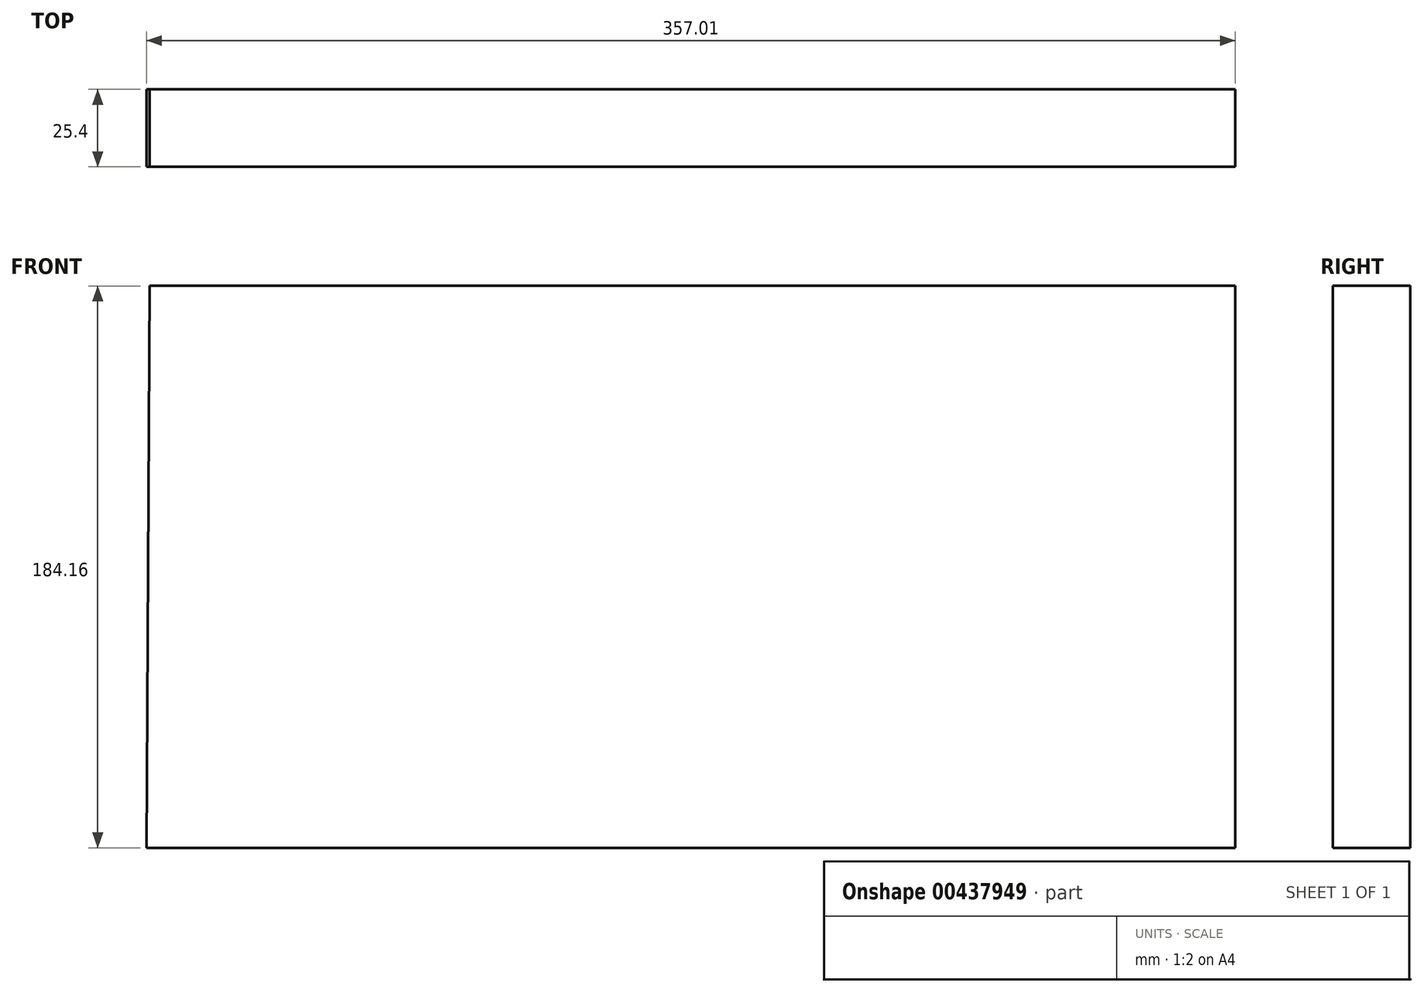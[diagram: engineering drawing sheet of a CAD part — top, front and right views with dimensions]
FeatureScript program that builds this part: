
annotation { "Feature Type Name" : "Feature", "Feature Type Description" : "" }
export const myFeature = defineFeature(function(context is Context, id is Id, definition is map)
    precondition{}
    {
        {
            var Q0;
            Q0=qCreatedBy(makeId("Front.planeOp"),FACE);
            var sketch = newSketch(context, id + "F0", { "sketchPlane" : qUnion([Q0])});
            skLineSegment(sketch, "E0.bottom", {"start": v(-163.17, 91.73) * mm, "end": v(192.83, 91.73) * mm});
            skLineSegment(sketch, "E0.top", {"start": v(-164.18, -92.43) * mm, "end": v(192.83, -92.43) * mm});
            skLineSegment(sketch, "E0.right", {"start": v(192.83, 91.73) * mm, "end": v(192.83, -92.43) * mm});
            skLineSegment(sketch, "E1", {"start": v(-163.17, 91.73) * mm, "end": v(-164.18, -92.43) * mm});
            skSolve(sketch);
        }
        {
            var Q0;
            {var subQ0=sQuery(id+"F0.wireOp",EDGE,"E0.bottom");Q0=makeQuery(id+"F0.imprint","IMPRINT",FACE,{"disambiguationData":[TD([[makeQuery(id+"F0.imprint","IMPRINT",EDGE,{"derivedFrom":subQ0}),-1.0]])]});}
            var sketch = newSketch(context, id + "F1", { "sketchPlane" : qUnion([Q0])});
            skSolve(sketch);
        }
        {
            var Q0;
            Q0 = qSketchRegion(id + "F1", true);
            var Q1;
            {var subQ0=sQuery(id+"F0.wireOp",EDGE,"aZiYQIyP-ZeOb-ANGz-mRzi-wyuS0cQEmIPq");Q1=makeQuery(id+"F0.imprint","IMPRINT",FACE,{"disambiguationData":[TD([[makeQuery(id+"F0.imprint","IMPRINT",EDGE,{"derivedFrom":subQ0}),-1.0]])]});}
            var Q2;
            Q2=makeQuery(id+"F1.imprint","IMPRINT",FACE,{"disambiguationData":[TD([[makeQuery(id+"F1.imprint","IMPRINT",EDGE,{"derivedFrom":makeQuery(id+"F0.imprint","IMPRINT",EDGE,{"derivedFrom":sQuery(id+"F0.wireOp",EDGE,"E0.bottom")})}),-1.0]])]});
            extrude(context, id + "F2", {"entities" : qUnion([Q0, Q1, Q2]), "depth" : 25.4 * mm, "offsetDistance" : 25.4 * mm});
        }
    });
